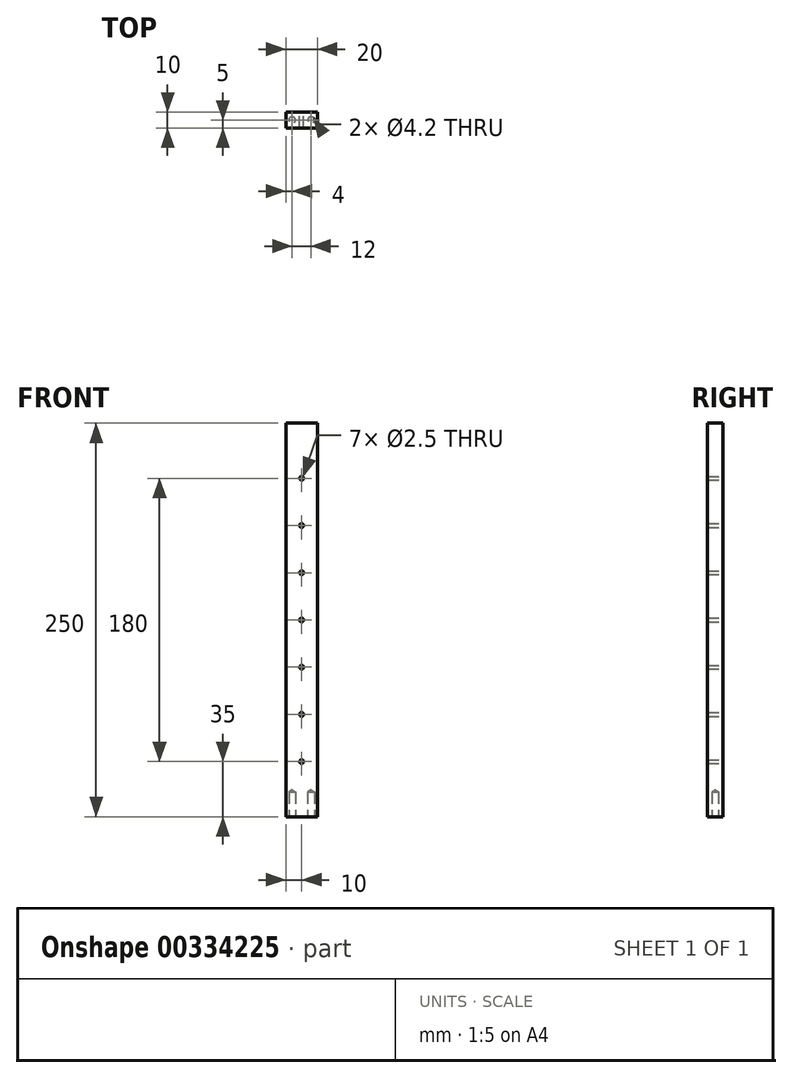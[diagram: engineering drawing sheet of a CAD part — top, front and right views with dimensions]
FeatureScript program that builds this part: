
annotation { "Feature Type Name" : "Feature", "Feature Type Description" : "" }
export const myFeature = defineFeature(function(context is Context, id is Id, definition is map)
    precondition{}
    {
        {
            var Q0;
            Q0=qCreatedBy(makeId("Front.planeOp"),FACE);
            var sketch = newSketch(context, id + "F0", { "sketchPlane" : qUnion([Q0])});
            skLineSegment(sketch, "E0", {"start": v(0, 29.34) * mm, "end": v(0, -32.9) * mm, "construction": true});
            skLineSegment(sketch, "E1", {"start": v(29.25, 0) * mm, "end": v(-31.12, 0) * mm, "construction": true});
            skLineSegment(sketch, "E2.bottom", {"start": v(-10, 125) * mm, "end": v(10, 125) * mm});
            skLineSegment(sketch, "E2.top", {"start": v(-10, -125) * mm, "end": v(10, -125) * mm});
            skLineSegment(sketch, "E2.left", {"start": v(-10, 125) * mm, "end": v(-10, -125) * mm});
            skLineSegment(sketch, "E2.right", {"start": v(10, 125) * mm, "end": v(10, -125) * mm});
            skSolve(sketch);
        }
        {
            var Q0;
            Q0 = qSketchRegion(id + "F0", true);
            extrude(context, id + "F1", {"entities" : qUnion([Q0]), "depth" : 10 * mm});
        }
        {
            var Q0;
            Q0=makeQuery(id+"F1.opExtrude","SWEPT_FACE",FACE,{"disambiguationData":[OSD([sQuery(id+"F0.wireOp",EDGE,"E2.top")])]});
            var sketch = newSketch(context, id + "F2", { "sketchPlane" : qUnion([Q0])});
            skLineSegment(sketch, "E3", {"start": v(-10, 5) * mm, "end": v(19.26, 5) * mm, "construction": true});
            skLineSegment(sketch, "E4", {"start": v(0, 25.9) * mm, "end": v(0, -10.15) * mm, "construction": true});
            skPoint(sketch, "E5", {"position": v(-6, 5) * mm});
            skPoint(sketch, "E6.MirrorP", {"position": v(6, 5) * mm});
            skSolve(sketch);
        }
        {
            var Q0;
            Q0=sQuery(id+"F2.wireOp",VERTEX,"E5");
            var Q1;
            Q1=sQuery(id+"F2.wireOp",VERTEX,"E6.MirrorP");
            var Q2;
            Q2=makeQuery(id+"F1.opExtrude","SWEPT_BODY",BODY,{"disambiguationData":[OSD([sQuery(id+"F0.wireOp",EDGE,"E2.bottom"),sQuery(id+"F0.wireOp",EDGE,"E2.top"),sQuery(id+"F0.wireOp",EDGE,"E2.left"),sQuery(id+"F0.wireOp",EDGE,"E2.right")])]});
            hole(context, id + "F3", {"style" : HoleStyle.SIMPLE, "endStyle" : HoleEndStyle.BLIND, "standardTappedOrClearance" : lookupTablePath({ "standard" : "ISO", "engagement" : "75%", "pitch" : "0.8 mm", "size" : "M5", "type" : "Tapped" }), "standardBlindInLast" : lookupTablePath({ "standard" : "ISO", "engagement" : "75%", "pitch" : "0.8 mm", "size" : "M5", "type" : "Tapped" }), "holeDiameter" : 4.2 * mm, "showTappedDepth" : true, "holeDepth" : 15.8 * mm, "tappedDepth" : 15 * mm, "tapClearance" : 1, "locations" : qUnion([Q0, Q1]), "scope" : qUnion([Q2]), "majorDiameter" : 5 * mm});
        }
        {
            var Q0;
            Q0=makeQuery(id+"F1.opExtrude","CAP_FACE",FACE,{"disambiguationData":[OSD([sQuery(id+"F0.wireOp",EDGE,"E2.bottom"),sQuery(id+"F0.wireOp",EDGE,"E2.top"),sQuery(id+"F0.wireOp",EDGE,"E2.left"),sQuery(id+"F0.wireOp",EDGE,"E2.right")])],"isStart":true});
            var sketch = newSketch(context, id + "F4", { "sketchPlane" : qUnion([Q0])});
            skLineSegment(sketch, "E7", {"start": v(0, 125) * mm, "end": v(0, -136.53) * mm, "construction": true});
            skLineSegment(sketch, "E8", {"start": v(72.38, 0) * mm, "end": v(-71.06, 0) * mm, "construction": true});
            skPoint(sketch, "E8.endSnap0", {"position": v(-10, 0) * mm});
            skPoint(sketch, "E9", {"position": v(0, 0) * mm});
            skPoint(sketch, "E10", {"position": v(0, 30) * mm});
            skPoint(sketch, "E11", {"position": v(0, 60) * mm});
            skPoint(sketch, "E12", {"position": v(0, 90) * mm});
            skPoint(sketch, "E13", {"position": v(0, -30) * mm});
            skPoint(sketch, "E14", {"position": v(0, -60) * mm});
            skPoint(sketch, "E15", {"position": v(0, -90) * mm});
            skSolve(sketch);
        }
        {
            var Q0;
            Q0=sQuery(id+"F4.wireOp",VERTEX,"E10");
            var Q1;
            Q1=sQuery(id+"F4.wireOp",VERTEX,"E11");
            var Q2;
            Q2=sQuery(id+"F4.wireOp",VERTEX,"E12");
            var Q3;
            Q3=sQuery(id+"F4.wireOp",VERTEX,"E9");
            var Q4;
            Q4=sQuery(id+"F4.wireOp",VERTEX,"E13");
            var Q5;
            Q5=sQuery(id+"F4.wireOp",VERTEX,"E14");
            var Q6;
            Q6=sQuery(id+"F4.wireOp",VERTEX,"E15");
            var Q7;
            Q7=makeQuery(id+"F1.opExtrude","SWEPT_BODY",BODY,{"disambiguationData":[OSD([sQuery(id+"F0.wireOp",EDGE,"E2.bottom"),sQuery(id+"F0.wireOp",EDGE,"E2.top"),sQuery(id+"F0.wireOp",EDGE,"E2.left"),sQuery(id+"F0.wireOp",EDGE,"E2.right")])]});
            hole(context, id + "F5", {"style" : HoleStyle.SIMPLE, "endStyle" : HoleEndStyle.BLIND, "standardTappedOrClearance" : lookupTablePath({ "standard" : "ISO", "engagement" : "75%", "pitch" : "0.5 mm", "size" : "M3", "type" : "Tapped" }), "standardBlindInLast" : lookupTablePath({ "standard" : "ISO", "engagement" : "75%", "pitch" : "0.5 mm", "size" : "M3", "type" : "Tapped" }), "holeDiameter" : 2.5 * mm, "showTappedDepth" : true, "holeDepth" : 15.5 * mm, "tappedDepth" : 15 * mm, "tapClearance" : 1, "locations" : qUnion([Q0, Q1, Q2, Q3, Q4, Q5, Q6]), "scope" : qUnion([Q7]), "majorDiameter" : 3 * mm});
        }
    });
